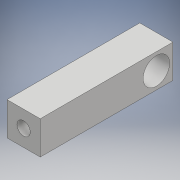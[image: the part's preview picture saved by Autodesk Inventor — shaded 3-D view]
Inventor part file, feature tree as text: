
AUTODESK INVENTOR PART (.ipt)
format: ipt  version: 2017 SP1 (Build 210196100, 196)  size: 109,056 bytes
history: native  units: mm
features: sketch x3, hole x2, extrude x1
ambient origin geometry x8: Origin, YZ Plane, XZ Plane, XY Plane, X Axis, Y Axis, Z Axis, Center Point
bodies: Solide1 (feature_tree)
feature tree (6):
  extrude  "Extrusion1"  Depth=10.0mm
  hole  "Perçage1"  [1 undecoded]
  hole  "Perçage2"  [1 undecoded]
  sketch  "Esquisse1"
  sketch  "Esquisse2"
  sketch  "Esquisse3"
note: 2 required parameter values undecoded (feature->parameter linkage not recoverable at this tier; creation-order binding heuristic only, values carry confidence <= 0.55)
